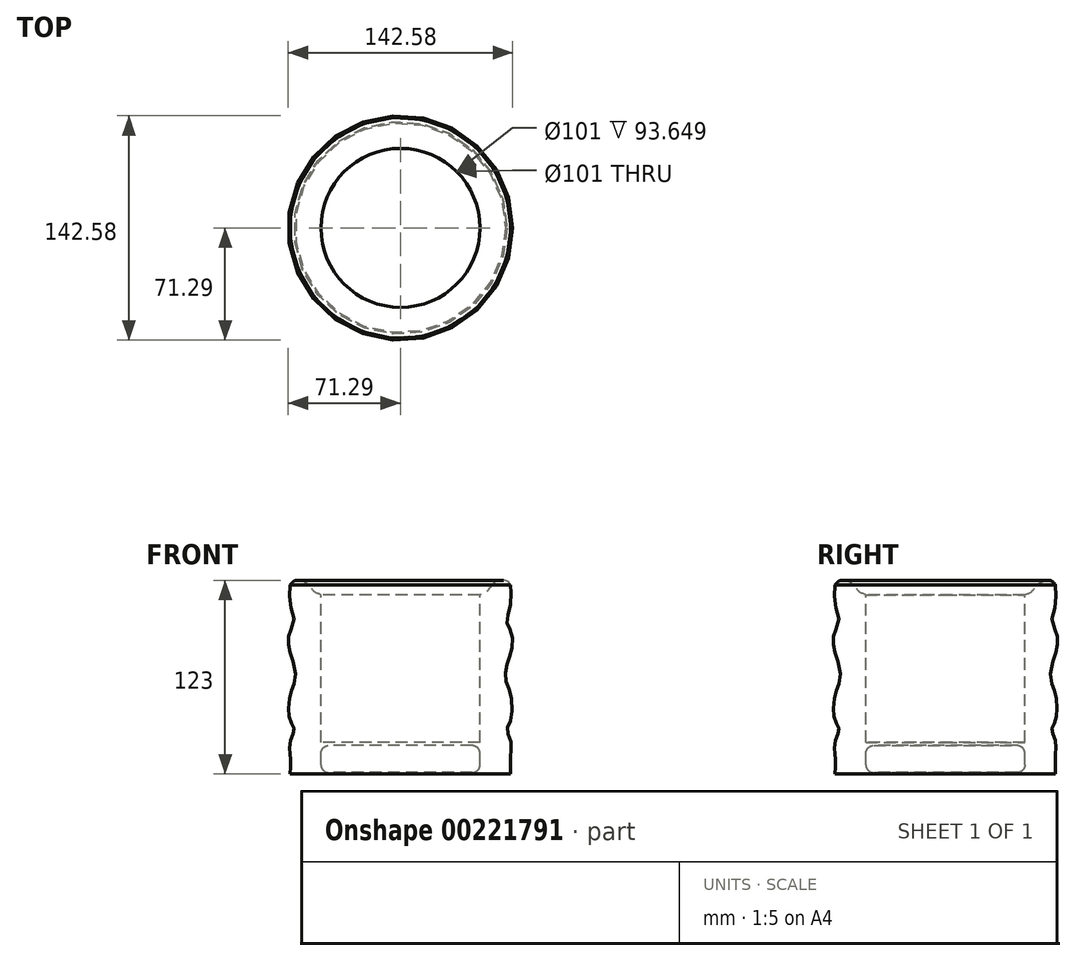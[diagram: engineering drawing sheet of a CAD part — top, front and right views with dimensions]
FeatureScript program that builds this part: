
annotation { "Feature Type Name" : "Feature", "Feature Type Description" : "" }
export const myFeature = defineFeature(function(context is Context, id is Id, definition is map)
    precondition{}
    {
        {
            var Q0;
            Q0=qCreatedBy(makeId("Front.planeOp"),FACE);
            var sketch = newSketch(context, id + "F0", { "sketchPlane" : qUnion([Q0])});
            skLineSegment(sketch, "E0", {"start": v(0, 0) * mm, "end": v(-70, 0) * mm});
            skFitSpline(sketch, "E1", {"points": [v(-70, 120) * mm, v(-70, 107.35) * mm, v(-67.47, 96.37) * mm, v(-70.76, 89.23) * mm, v(-70, 76.78) * mm, v(-67.41, 68.58) * mm, v(-67.09, 58.94) * mm, v(-70, 50.54) * mm, v(-70, 33.87) * mm, v(-67.65, 28.61) * mm, v(-70, 20.52) * mm, v(-70, 12.82) * mm, v(-69.9, 7.33) * mm, v(-70, 3.43) * mm, v(-70, 0) * mm], "startDerivative": vector(-0.92, -61.54) * mm, "endDerivative": vector(14.1, -71) * mm});
            skLineSegment(sketch, "E2", {"start": v(0, 20) * mm, "end": v(-50.5, 20) * mm});
            skLineSegment(sketch, "E3", {"start": v(-50.5, 20) * mm, "end": v(-50.5, 113.65) * mm});
            skFitSpline(sketch, "E4", {"points": [v(-70, 120) * mm, v(-66.2, 122.93) * mm, v(-58.15, 120) * mm, v(-54.77, 115.78) * mm, v(-50.5, 113.65) * mm], "startDerivative": vector(13.1, 16.93) * mm, "endDerivative": vector(14.94, -8.97) * mm});
            skLineSegment(sketch, "E5", {"start": v(0, 18) * mm, "end": v(-45.5, 18) * mm});
            skLineSegment(sketch, "E6", {"start": v(-50.5, 13) * mm, "end": v(-50.5, 5.8) * mm});
            skLineSegment(sketch, "E7", {"start": v(-45.5, 0.8) * mm, "end": v(0, 0.8) * mm});
            skLineSegment(sketch, "E8", {"start": v(0, 20) * mm, "end": v(0, 18) * mm});
            skLineSegment(sketch, "E9", {"start": v(0, 0.8) * mm, "end": v(0, 0) * mm});
            skPoint(sketch, "E10.visualSharp", {"position": v(-50.5, 18) * mm});
            skArc(sketch, "E10.filletArc", {"start": v(-45.5, 18) * mm, "mid": v(-49.03, 16.54) * mm, "end": v(-50.5, 13) * mm});
            skPoint(sketch, "E11.visualSharp", {"position": v(-50.5, 0.8) * mm});
            skArc(sketch, "E11.filletArc", {"start": v(-50.5, 5.8) * mm, "mid": v(-49.03, 2.26) * mm, "end": v(-45.5, 0.8) * mm});
            skSolve(sketch);
        }
        {
            var Q0;
            Q0=makeQuery(id+"F0.imprint","IMPRINT",FACE,{"disambiguationData":[TD([[makeQuery(id+"F0.imprint","IMPRINT",EDGE,{"derivedFrom":sQuery(id+"F0.wireOp",EDGE,"E0")}),-1.0]])]});
            var Q1;
            Q1=sQuery(id+"F0.wireOp",EDGE,"E8");
            revolve(context, id + "F1", {"entities" : qUnion([Q0]), "axis" : qUnion([Q1]), "revolveType" : RevolveType.FULL});
        }
    });
